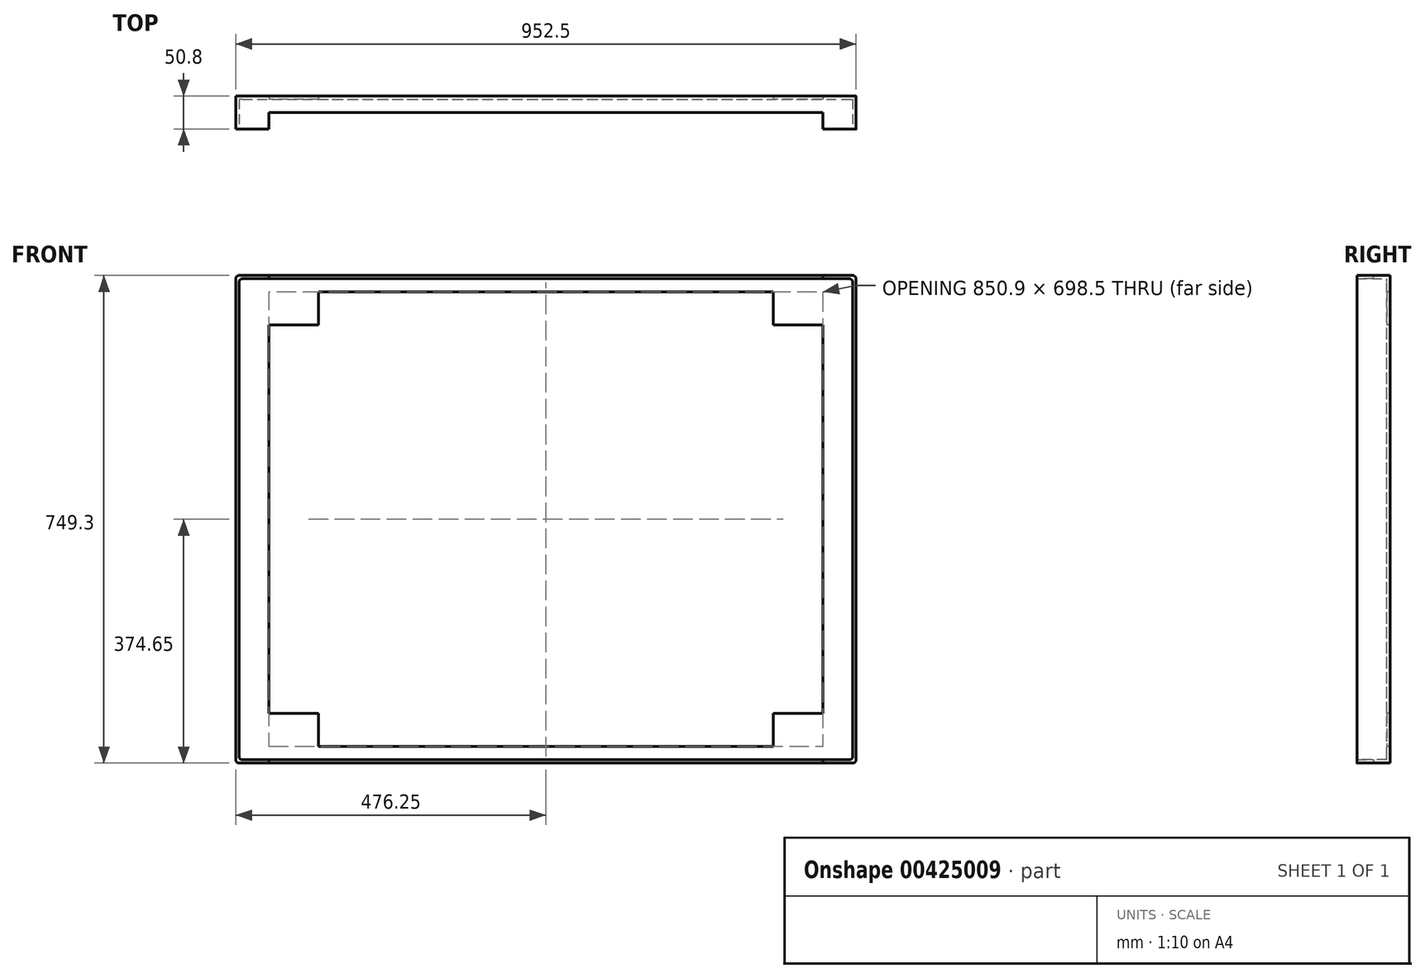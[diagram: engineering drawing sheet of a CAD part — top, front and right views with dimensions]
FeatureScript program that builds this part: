
annotation { "Feature Type Name" : "Feature", "Feature Type Description" : "" }
export const myFeature = defineFeature(function(context is Context, id is Id, definition is map)
    precondition{}
    {
        {
            var Q0;
            Q0=qCreatedBy(makeId("Front.planeOp"),FACE);
            var sketch = newSketch(context, id + "F0", { "sketchPlane" : qUnion([Q0])});
            skLineSegment(sketch, "E0", {"start": v(0, 0) * mm, "end": v(0, 749.3) * mm});
            skLineSegment(sketch, "E1", {"start": v(0, 749.3) * mm, "end": v(952.5, 749.3) * mm});
            skLineSegment(sketch, "E2", {"start": v(952.5, 749.3) * mm, "end": v(952.5, 0) * mm});
            skLineSegment(sketch, "E3", {"start": v(952.5, 0) * mm, "end": v(0, 0) * mm});
            skLineSegment(sketch, "E4.0", {"start": v(50.8, 25.4) * mm, "end": v(50.8, 723.9) * mm});
            skLineSegment(sketch, "E5.0", {"start": v(901.7, 723.9) * mm, "end": v(901.7, 25.4) * mm});
            skLineSegment(sketch, "E6.0", {"start": v(50.8, 723.9) * mm, "end": v(901.7, 723.9) * mm});
            skLineSegment(sketch, "E7.0", {"start": v(901.7, 25.4) * mm, "end": v(50.8, 25.4) * mm});
            skLineSegment(sketch, "E8", {"start": v(952.5, 749.3) * mm, "end": v(901.7, 698.5) * mm});
            skLineSegment(sketch, "E9", {"start": v(952.5, 0) * mm, "end": v(901.7, 50.8) * mm});
            skLineSegment(sketch, "E10", {"start": v(0, 0) * mm, "end": v(50.8, 50.8) * mm});
            skLineSegment(sketch, "E11", {"start": v(0, 749.3) * mm, "end": v(50.8, 698.5) * mm});
            skLineSegment(sketch, "E12", {"start": v(901.7, 723.9) * mm, "end": v(901.7, 749.3) * mm});
            skLineSegment(sketch, "E13", {"start": v(901.7, 25.4) * mm, "end": v(901.7, 0) * mm});
            skLineSegment(sketch, "E14", {"start": v(50.8, 25.4) * mm, "end": v(50.8, 0) * mm});
            skLineSegment(sketch, "E15", {"start": v(50.8, 723.9) * mm, "end": v(50.8, 749.3) * mm});
            skSolve(sketch);
        }
        {
            var Q0;
            Q0=qSketchRegion(id+"F0",true);
            extrude(context, id + "F1", {"entities" : qUnion([Q0]), "depth" : 5.08 * mm});
        }
        {
            var Q0;
            Q0=makeQuery(id+"F1.opExtrude","SWEPT_FACE",FACE,{"disambiguationData":[OSD([sQuery(id+"F0.wireOp",EDGE,"E3")])]});
            var sketch = newSketch(context, id + "F2", { "sketchPlane" : qUnion([Q0])});
            skLineSegment(sketch, "E16", {"start": v(0, 0) * mm, "end": v(0, 50.8) * mm});
            skLineSegment(sketch, "E17", {"start": v(0, 50.8) * mm, "end": v(50.8, 50.8) * mm});
            skLineSegment(sketch, "E18", {"start": v(50.8, 50.8) * mm, "end": v(50.8, 25.4) * mm});
            skLineSegment(sketch, "E19", {"start": v(50.8, 25.4) * mm, "end": v(901.7, 25.4) * mm});
            skLineSegment(sketch, "E20", {"start": v(901.7, 25.4) * mm, "end": v(901.7, 50.8) * mm});
            skLineSegment(sketch, "E21", {"start": v(901.7, 50.8) * mm, "end": v(952.5, 50.8) * mm});
            skLineSegment(sketch, "E22", {"start": v(952.5, 50.8) * mm, "end": v(952.5, 0) * mm});
            skLineSegment(sketch, "E23", {"start": v(952.5, 0) * mm, "end": v(0, 0) * mm});
            skSolve(sketch);
        }
        {
            var Q0;
            Q0=qSketchRegion(id+"F2",true);
            extrude(context, id + "F3", {"entities" : qUnion([Q0]), "operationType" : NewBodyOperationType.ADD, "oppositeDirection" : true, "depth" : 5.08 * mm});
        }
        {
            var Q0;
            Q0=makeQuery(id+"F1.opExtrude","SWEPT_FACE",FACE,{"disambiguationData":[OSD([sQuery(id+"F0.wireOp",EDGE,"E1")])]});
            var sketch = newSketch(context, id + "F4", { "sketchPlane" : qUnion([Q0])});
            skLineSegment(sketch, "E24", {"start": v(0, 0) * mm, "end": v(0, -50.8) * mm});
            skLineSegment(sketch, "E25", {"start": v(0, -50.8) * mm, "end": v(50.8, -50.8) * mm});
            skLineSegment(sketch, "E26", {"start": v(50.8, -50.8) * mm, "end": v(50.8, -25.4) * mm});
            skLineSegment(sketch, "E27", {"start": v(50.8, -25.4) * mm, "end": v(901.7, -25.4) * mm});
            skLineSegment(sketch, "E28", {"start": v(901.7, -25.4) * mm, "end": v(901.7, -50.8) * mm});
            skLineSegment(sketch, "E29", {"start": v(901.7, -50.8) * mm, "end": v(952.5, -50.8) * mm});
            skLineSegment(sketch, "E30", {"start": v(952.5, -50.8) * mm, "end": v(952.5, 0) * mm});
            skLineSegment(sketch, "E31", {"start": v(952.5, 0) * mm, "end": v(0, 0) * mm});
            skSolve(sketch);
        }
        {
            var Q0;
            Q0=qSketchRegion(id+"F4",true);
            extrude(context, id + "F5", {"entities" : qUnion([Q0]), "operationType" : NewBodyOperationType.ADD, "oppositeDirection" : true, "depth" : 5.08 * mm});
        }
        {
            var Q0;
            Q0=makeQuery(id+"F5.boolean.opBoolean","MERGE",FACE,{"derivedFrom":[makeQuery(id+"F3.boolean.opBoolean","MERGE",FACE,{"derivedFrom":[makeQuery(id+"F1.opExtrude","SWEPT_FACE",FACE,{"disambiguationData":[OSD([sQuery(id+"F0.wireOp",EDGE,"E0")])]}),makeQuery(id+"F3.opExtrude","SWEPT_FACE",FACE,{"disambiguationData":[OSD([sQuery(id+"F2.wireOp",EDGE,"E16")])]})]}),makeQuery(id+"F5.opExtrude","SWEPT_FACE",FACE,{"disambiguationData":[OSD([sQuery(id+"F4.wireOp",EDGE,"E24")])]})]});
            var sketch = newSketch(context, id + "F6", { "sketchPlane" : qUnion([Q0])});
            skLineSegment(sketch, "E32", {"start": v(0, 0) * mm, "end": v(50.8, 0) * mm});
            skLineSegment(sketch, "E33", {"start": v(50.8, 0) * mm, "end": v(50.8, 749.3) * mm});
            skLineSegment(sketch, "E34", {"start": v(50.8, 749.3) * mm, "end": v(0.25, 744.22) * mm});
            skLineSegment(sketch, "E35", {"start": v(0.25, 744.22) * mm, "end": v(0.25, -5.08) * mm});
            skSolve(sketch);
        }
        {
            var Q0;
            Q0=qSketchRegion(id+"F6",true);
            extrude(context, id + "F7", {"entities" : qUnion([Q0]), "operationType" : NewBodyOperationType.ADD, "oppositeDirection" : true, "depth" : 5.08 * mm});
        }
        {
            var Q0;
            Q0=makeQuery(id+"F5.boolean.opBoolean","MERGE",FACE,{"derivedFrom":[makeQuery(id+"F3.boolean.opBoolean","MERGE",FACE,{"derivedFrom":[makeQuery(id+"F1.opExtrude","SWEPT_FACE",FACE,{"disambiguationData":[OSD([sQuery(id+"F0.wireOp",EDGE,"E2")])]}),makeQuery(id+"F3.opExtrude","SWEPT_FACE",FACE,{"disambiguationData":[OSD([sQuery(id+"F2.wireOp",EDGE,"E22")])]})]}),makeQuery(id+"F5.opExtrude","SWEPT_FACE",FACE,{"disambiguationData":[OSD([sQuery(id+"F4.wireOp",EDGE,"E30")])]})]});
            var sketch = newSketch(context, id + "F8", { "sketchPlane" : qUnion([Q0])});
            skLineSegment(sketch, "E36", {"start": v(0, 0) * mm, "end": v(-50.8, 0) * mm});
            skLineSegment(sketch, "E37", {"start": v(-50.8, 0) * mm, "end": v(-50.8, 749.3) * mm});
            skLineSegment(sketch, "E38", {"start": v(-50.8, 749.3) * mm, "end": v(0, 749.3) * mm});
            skLineSegment(sketch, "E39", {"start": v(0, 749.3) * mm, "end": v(0, 0) * mm});
            skSolve(sketch);
        }
        {
            var Q0;
            Q0=qSketchRegion(id+"F8",true);
            extrude(context, id + "F9", {"entities" : qUnion([Q0]), "operationType" : NewBodyOperationType.ADD, "oppositeDirection" : true, "depth" : 5.08 * mm});
        }
        {
            var Q0;
            Q0=makeQuery(id+"F3.boolean.opBoolean","MERGE",EDGE,{"derivedFrom":[makeQuery(id+"F1.opExtrude","SWEPT_EDGE",EDGE,{"disambiguationData":[OSD([sQuery(id+"F0.wireOp",EDGE,"E0"),sQuery(id+"F0.wireOp",EDGE,"E3"),sQuery(id+"F0.wireOp",EDGE,"E10")])]}),makeQuery(id+"F3.opExtrude","CAP_EDGE",EDGE,{"disambiguationData":[OSD([sQuery(id+"F2.wireOp",EDGE,"E16")])],"isStart":true})]});
            var Q1;
            Q1=makeQuery(id+"F7.boolean.opBoolean","INTERSECT",EDGE,{"derivedFrom":[makeQuery(id+"F3.opExtrude","CAP_FACE",FACE,{"disambiguationData":[OSD([sQuery(id+"F2.wireOp",EDGE,"E16"),sQuery(id+"F2.wireOp",EDGE,"E17"),sQuery(id+"F2.wireOp",EDGE,"E18"),sQuery(id+"F2.wireOp",EDGE,"E19"),sQuery(id+"F2.wireOp",EDGE,"E20"),sQuery(id+"F2.wireOp",EDGE,"E21"),sQuery(id+"F2.wireOp",EDGE,"E22"),sQuery(id+"F2.wireOp",EDGE,"E23")])],"isStart":false}),makeQuery(id+"F7.opExtrude","CAP_FACE",FACE,{"disambiguationData":[OSD([sQuery(id+"F6.wireOp",EDGE,"E32"),sQuery(id+"F6.wireOp",EDGE,"E33"),sQuery(id+"F6.wireOp",EDGE,"E34"),sQuery(id+"F6.wireOp",EDGE,"E35")])],"isStart":false})]});
            var Q2;
            Q2=makeQuery(id+"F7.boolean.opBoolean","INTERSECT",EDGE,{"derivedFrom":[makeQuery(id+"F5.opExtrude","CAP_FACE",FACE,{"disambiguationData":[OSD([sQuery(id+"F4.wireOp",EDGE,"E24"),sQuery(id+"F4.wireOp",EDGE,"E25"),sQuery(id+"F4.wireOp",EDGE,"E26"),sQuery(id+"F4.wireOp",EDGE,"E27"),sQuery(id+"F4.wireOp",EDGE,"E28"),sQuery(id+"F4.wireOp",EDGE,"E29"),sQuery(id+"F4.wireOp",EDGE,"E30"),sQuery(id+"F4.wireOp",EDGE,"E31")])],"isStart":false}),makeQuery(id+"F7.opExtrude","CAP_FACE",FACE,{"disambiguationData":[OSD([sQuery(id+"F6.wireOp",EDGE,"E32"),sQuery(id+"F6.wireOp",EDGE,"E33"),sQuery(id+"F6.wireOp",EDGE,"E34"),sQuery(id+"F6.wireOp",EDGE,"E35")])],"isStart":false})]});
            var Q3;
            Q3=makeQuery(id+"F5.boolean.opBoolean","MERGE",EDGE,{"derivedFrom":[makeQuery(id+"F1.opExtrude","SWEPT_EDGE",EDGE,{"disambiguationData":[OSD([sQuery(id+"F0.wireOp",EDGE,"E0"),sQuery(id+"F0.wireOp",EDGE,"E1"),sQuery(id+"F0.wireOp",EDGE,"E11")])]}),makeQuery(id+"F5.opExtrude","CAP_EDGE",EDGE,{"disambiguationData":[OSD([sQuery(id+"F4.wireOp",EDGE,"E24")])],"isStart":true})]});
            var Q4;
            Q4=makeQuery(id+"F5.boolean.opBoolean","MERGE",EDGE,{"derivedFrom":[makeQuery(id+"F1.opExtrude","SWEPT_EDGE",EDGE,{"disambiguationData":[OSD([sQuery(id+"F0.wireOp",EDGE,"E1"),sQuery(id+"F0.wireOp",EDGE,"E2"),sQuery(id+"F0.wireOp",EDGE,"E8")])]}),makeQuery(id+"F5.opExtrude","CAP_EDGE",EDGE,{"disambiguationData":[OSD([sQuery(id+"F4.wireOp",EDGE,"E30")])],"isStart":true})]});
            var Q5;
            Q5=makeQuery(id+"F9.boolean.opBoolean","INTERSECT",EDGE,{"derivedFrom":[makeQuery(id+"F5.opExtrude","CAP_FACE",FACE,{"disambiguationData":[OSD([sQuery(id+"F4.wireOp",EDGE,"E24"),sQuery(id+"F4.wireOp",EDGE,"E25"),sQuery(id+"F4.wireOp",EDGE,"E26"),sQuery(id+"F4.wireOp",EDGE,"E27"),sQuery(id+"F4.wireOp",EDGE,"E28"),sQuery(id+"F4.wireOp",EDGE,"E29"),sQuery(id+"F4.wireOp",EDGE,"E30"),sQuery(id+"F4.wireOp",EDGE,"E31")])],"isStart":false}),makeQuery(id+"F9.opExtrude","CAP_FACE",FACE,{"disambiguationData":[OSD([sQuery(id+"F8.wireOp",EDGE,"E36"),sQuery(id+"F8.wireOp",EDGE,"E37"),sQuery(id+"F8.wireOp",EDGE,"E38"),sQuery(id+"F8.wireOp",EDGE,"E39")])],"isStart":false})]});
            var Q6;
            Q6=makeQuery(id+"F3.boolean.opBoolean","MERGE",EDGE,{"derivedFrom":[makeQuery(id+"F1.opExtrude","SWEPT_EDGE",EDGE,{"disambiguationData":[OSD([sQuery(id+"F0.wireOp",EDGE,"E2"),sQuery(id+"F0.wireOp",EDGE,"E3"),sQuery(id+"F0.wireOp",EDGE,"E9")])]}),makeQuery(id+"F3.opExtrude","CAP_EDGE",EDGE,{"disambiguationData":[OSD([sQuery(id+"F2.wireOp",EDGE,"E22")])],"isStart":true})]});
            var Q7;
            Q7=makeQuery(id+"F9.boolean.opBoolean","INTERSECT",EDGE,{"derivedFrom":[makeQuery(id+"F3.opExtrude","CAP_FACE",FACE,{"disambiguationData":[OSD([sQuery(id+"F2.wireOp",EDGE,"E16"),sQuery(id+"F2.wireOp",EDGE,"E17"),sQuery(id+"F2.wireOp",EDGE,"E18"),sQuery(id+"F2.wireOp",EDGE,"E19"),sQuery(id+"F2.wireOp",EDGE,"E20"),sQuery(id+"F2.wireOp",EDGE,"E21"),sQuery(id+"F2.wireOp",EDGE,"E22"),sQuery(id+"F2.wireOp",EDGE,"E23")])],"isStart":false}),makeQuery(id+"F9.opExtrude","CAP_FACE",FACE,{"disambiguationData":[OSD([sQuery(id+"F8.wireOp",EDGE,"E36"),sQuery(id+"F8.wireOp",EDGE,"E37"),sQuery(id+"F8.wireOp",EDGE,"E38"),sQuery(id+"F8.wireOp",EDGE,"E39")])],"isStart":false})]});
            fillet(context, id + "F10", {"entities" : qUnion([Q0, Q1, Q2, Q3, Q4, Q5, Q6, Q7]), "radius" : 5.08 * mm, "tangentPropagation" : true, "allowEdgeOverflow" : false});
        }
        {
            var Q0;
            Q0=makeQuery(id+"F1.opExtrude","CAP_FACE",FACE,{"disambiguationData":[OSD([sQuery(id+"F0.wireOp",EDGE,"E0"),sQuery(id+"F0.wireOp",EDGE,"E1"),sQuery(id+"F0.wireOp",EDGE,"E2"),sQuery(id+"F0.wireOp",EDGE,"E3"),sQuery(id+"F0.wireOp",EDGE,"E4.0"),sQuery(id+"F0.wireOp",EDGE,"E5.0"),sQuery(id+"F0.wireOp",EDGE,"E6.0"),sQuery(id+"F0.wireOp",EDGE,"E7.0")])],"isStart":false});
            var sketch = newSketch(context, id + "F11", { "sketchPlane" : qUnion([Q0])});
            skLineSegment(sketch, "E40", {"start": v(901.7, 723.9) * mm, "end": v(901.7, 673.1) * mm});
            skLineSegment(sketch, "E41", {"start": v(901.7, 673.1) * mm, "end": v(825.5, 673.1) * mm});
            skLineSegment(sketch, "E42", {"start": v(825.5, 673.1) * mm, "end": v(825.5, 723.9) * mm});
            skLineSegment(sketch, "E43", {"start": v(825.5, 723.9) * mm, "end": v(901.7, 723.9) * mm});
            skLineSegment(sketch, "E44", {"start": v(901.7, 25.4) * mm, "end": v(901.7, 76.2) * mm});
            skLineSegment(sketch, "E45", {"start": v(901.7, 76.2) * mm, "end": v(825.5, 76.2) * mm});
            skLineSegment(sketch, "E46", {"start": v(825.5, 76.2) * mm, "end": v(825.5, 25.4) * mm});
            skLineSegment(sketch, "E47", {"start": v(825.5, 25.4) * mm, "end": v(901.7, 25.4) * mm});
            skLineSegment(sketch, "E48", {"start": v(50.8, 25.4) * mm, "end": v(127, 25.4) * mm});
            skLineSegment(sketch, "E49", {"start": v(127, 25.4) * mm, "end": v(127, 76.2) * mm});
            skLineSegment(sketch, "E50", {"start": v(127, 76.2) * mm, "end": v(50.8, 76.2) * mm});
            skLineSegment(sketch, "E51", {"start": v(50.8, 76.2) * mm, "end": v(50.8, 25.4) * mm});
            skLineSegment(sketch, "E52", {"start": v(50.8, 723.9) * mm, "end": v(127, 723.9) * mm});
            skLineSegment(sketch, "E53", {"start": v(127, 723.9) * mm, "end": v(127, 673.1) * mm});
            skLineSegment(sketch, "E54", {"start": v(127, 673.1) * mm, "end": v(50.8, 673.1) * mm});
            skLineSegment(sketch, "E55", {"start": v(50.8, 673.1) * mm, "end": v(50.8, 723.9) * mm});
            skSolve(sketch);
        }
        {
            var Q0;
            Q0=qSketchRegion(id+"F11",true);
            extrude(context, id + "F12", {"entities" : qUnion([Q0]), "operationType" : NewBodyOperationType.ADD, "oppositeDirection" : true, "depth" : 5.08 * mm});
        }
    });
